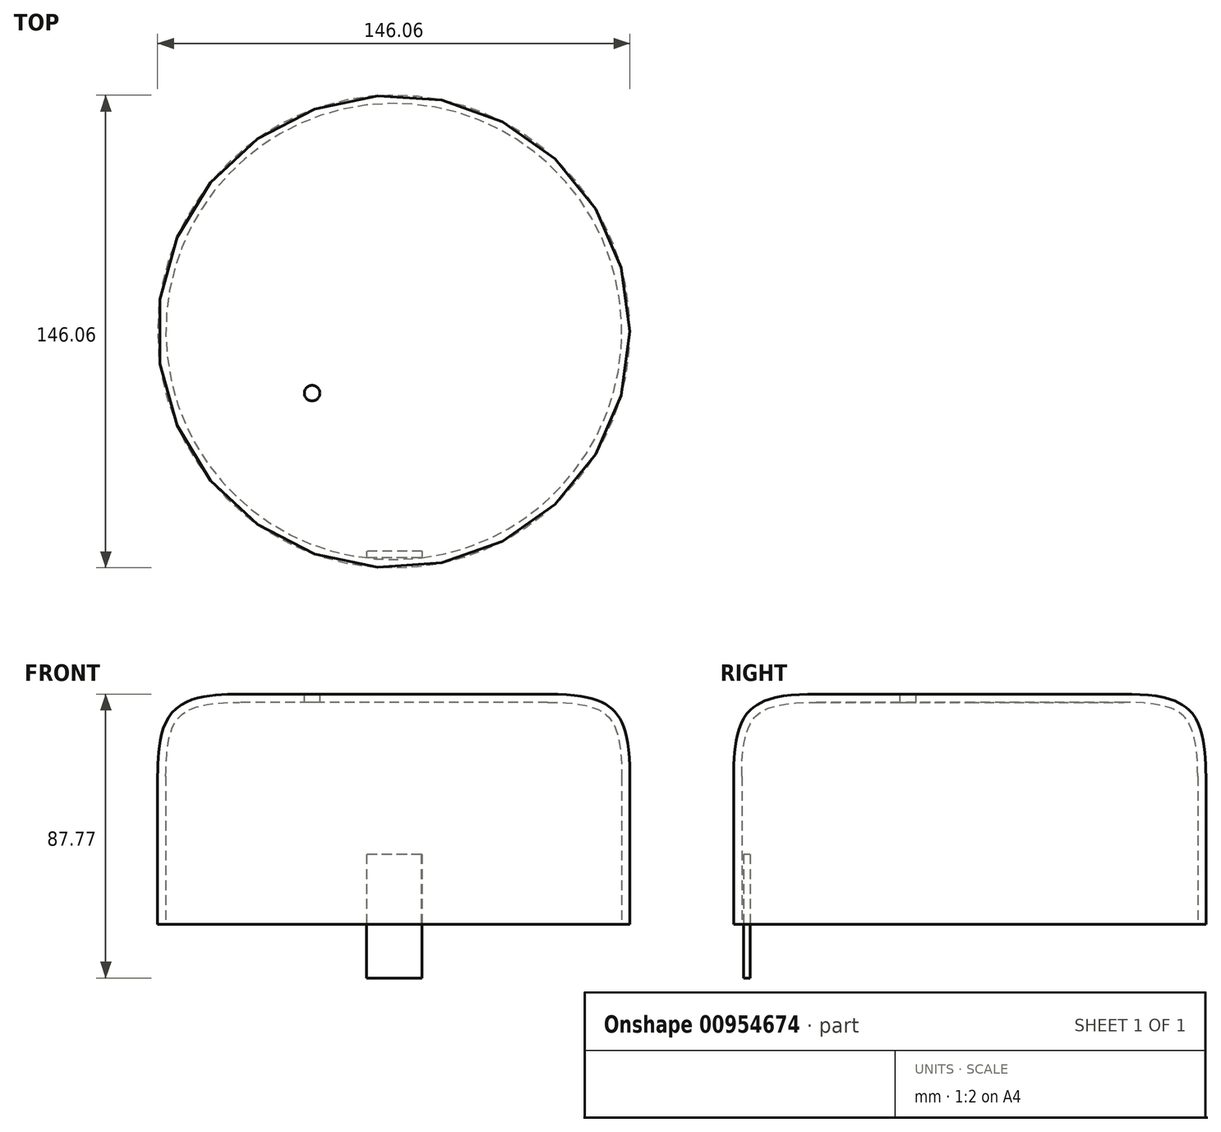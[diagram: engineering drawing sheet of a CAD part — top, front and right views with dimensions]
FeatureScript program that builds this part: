
annotation { "Feature Type Name" : "Feature", "Feature Type Description" : "" }
export const myFeature = defineFeature(function(context is Context, id is Id, definition is map)
    precondition{}
    {
        {
            var Q0;
            Q0=qCreatedBy(makeId("Top.planeOp"),FACE);
            cPlane(context, id + "F0", {"entities" : qUnion([Q0]), "cplaneType" : CPlaneType.OFFSET, "offset" : 0 * mm, "width" : 152.4 * mm, "height" : 152.4 * mm});
        }
        {
            var Q0;
            Q0=qCreatedBy(id+"F0.planeOp",FACE);
            var sketch = newSketch(context, id + "F1", { "sketchPlane" : qUnion([Q0])});
            skCircle(sketch, "E0", {"center": v(0, 0) * mm, "radius": 73.03 * mm});
            skSolve(sketch);
        }
        {
            var Q0;
            Q0=makeQuery(id+"F1.imprint","IMPRINT",FACE,{"disambiguationData":[TD([[makeQuery(id+"F1.imprint","IMPRINT",EDGE,{"derivedFrom":sQuery(id+"F1.wireOp",EDGE,"E0")}),1.0]])]});
            var Q1;
            Q1 = qSketchRegion(id + "F1", true);
            extrude(context, id + "F2", {"entities" : qUnion([Q0, Q1]), "endBound" : BoundingType.SYMMETRIC, "depth" : 71.12 * mm, "offsetDistance" : 25.4 * mm});
        }
        {
            var Q0;
            Q0=makeQuery(id+"F2.opExtrude","CAP_FACE",FACE,{"disambiguationData":[OSD([sQuery(id+"F1.wireOp",EDGE,"E0")])],"isStart":false});
            var Q1;
            Q1=makeQuery(id+"F2.opExtrude","CAP_EDGE",EDGE,{"disambiguationData":[OSD([sQuery(id+"F1.wireOp",EDGE,"E0")])],"isStart":false});
            fillet(context, id + "F3", {"entities" : qUnion([Q0, Q1]), "radius" : 25.4 * mm, "tangentPropagation" : true, "rho" : .6, "crossSection" : FilletCrossSection.CONIC, "allowEdgeOverflow" : false});
        }
        {
            var Q0;
            Q0=makeQuery(id+"F2.opExtrude","CAP_FACE",FACE,{"disambiguationData":[OSD([sQuery(id+"F1.wireOp",EDGE,"E0")])],"isStart":true});
            shell(context, id + "F4", {"entities" : qUnion([Q0]), "thickness" : 2.54 * mm});
        }
        {
            var Q0;
            Q0=makeQuery(id+"F2.opExtrude","CAP_FACE",FACE,{"disambiguationData":[OSD([sQuery(id+"F1.wireOp",EDGE,"E0")])],"isStart":false});
            var sketch = newSketch(context, id + "F5", { "sketchPlane" : qUnion([Q0])});
            skEllipse(sketch, "E1", {"center": v(-25.26, -19.05) * mm, "majorRadius": 6.76 * mm, "minorRadius": 2.45 * mm, "majorAxis": v(0.72, 0.7)});
            skSolve(sketch);
        }
        {
            var Q0;
            Q0=sQuery(id+"F5.wireOp",VERTEX,"E1.center");
            var Q1;
            Q1=makeQuery(id+"F2.opExtrude","SWEPT_BODY",BODY,{"disambiguationData":[OSD([sQuery(id+"F1.wireOp",EDGE,"E0")])]});
            hole(context, id + "F6", {"style" : HoleStyle.SIMPLE, "endStyle" : HoleEndStyle.THROUGH, "holeDiameter" : 4.83 * mm, "majorDiameter" : 6.35 * mm, "isTappedThrough" : true, "tappedDepth" : 12.7 * mm, "tapClearance" : 3, "locations" : qUnion([Q0]), "scope" : qUnion([Q1])});
        }
        {
            var Q0;
            Q0=qCreatedBy(makeId("Front.planeOp"),FACE);
            cPlane(context, id + "F7", {"entities" : qUnion([Q0]), "cplaneType" : CPlaneType.OFFSET, "offset" : 69.98 * mm, "width" : 152.4 * mm, "height" : 152.4 * mm});
        }
        {
            var Q0;
            Q0=qCreatedBy(id+"F7.planeOp",FACE);
            var sketch = newSketch(context, id + "F8", { "sketchPlane" : qUnion([Q0])});
            skLineSegment(sketch, "E2.bottom", {"start": v(8.68, -14) * mm, "end": v(-8.43, -14) * mm});
            skLineSegment(sketch, "E2.top", {"start": v(8.68, -52.2) * mm, "end": v(-8.43, -52.2) * mm});
            skLineSegment(sketch, "E2.left", {"start": v(8.68, -14) * mm, "end": v(8.68, -52.2) * mm});
            skLineSegment(sketch, "E2.right", {"start": v(-8.43, -14) * mm, "end": v(-8.43, -52.2) * mm});
            skSolve(sketch);
        }
        {
            var Q0;
            Q0 = qSketchRegion(id + "F8", true);
            extrude(context, id + "F9", {"entities" : qUnion([Q0]), "operationType" : NewBodyOperationType.ADD, "oppositeDirection" : true, "depth" : 2.03 * mm, "offsetDistance" : 25.4 * mm});
        }
        {
            var Q0;
            Q0=qCreatedBy(makeId("Front.planeOp"),FACE);
            cPlane(context, id + "F10", {"entities" : qUnion([Q0]), "cplaneType" : CPlaneType.OFFSET, "offset" : 67.82 * mm, "oppositeDirection" : true, "width" : 152.4 * mm, "height" : 152.4 * mm});
        }
    });
